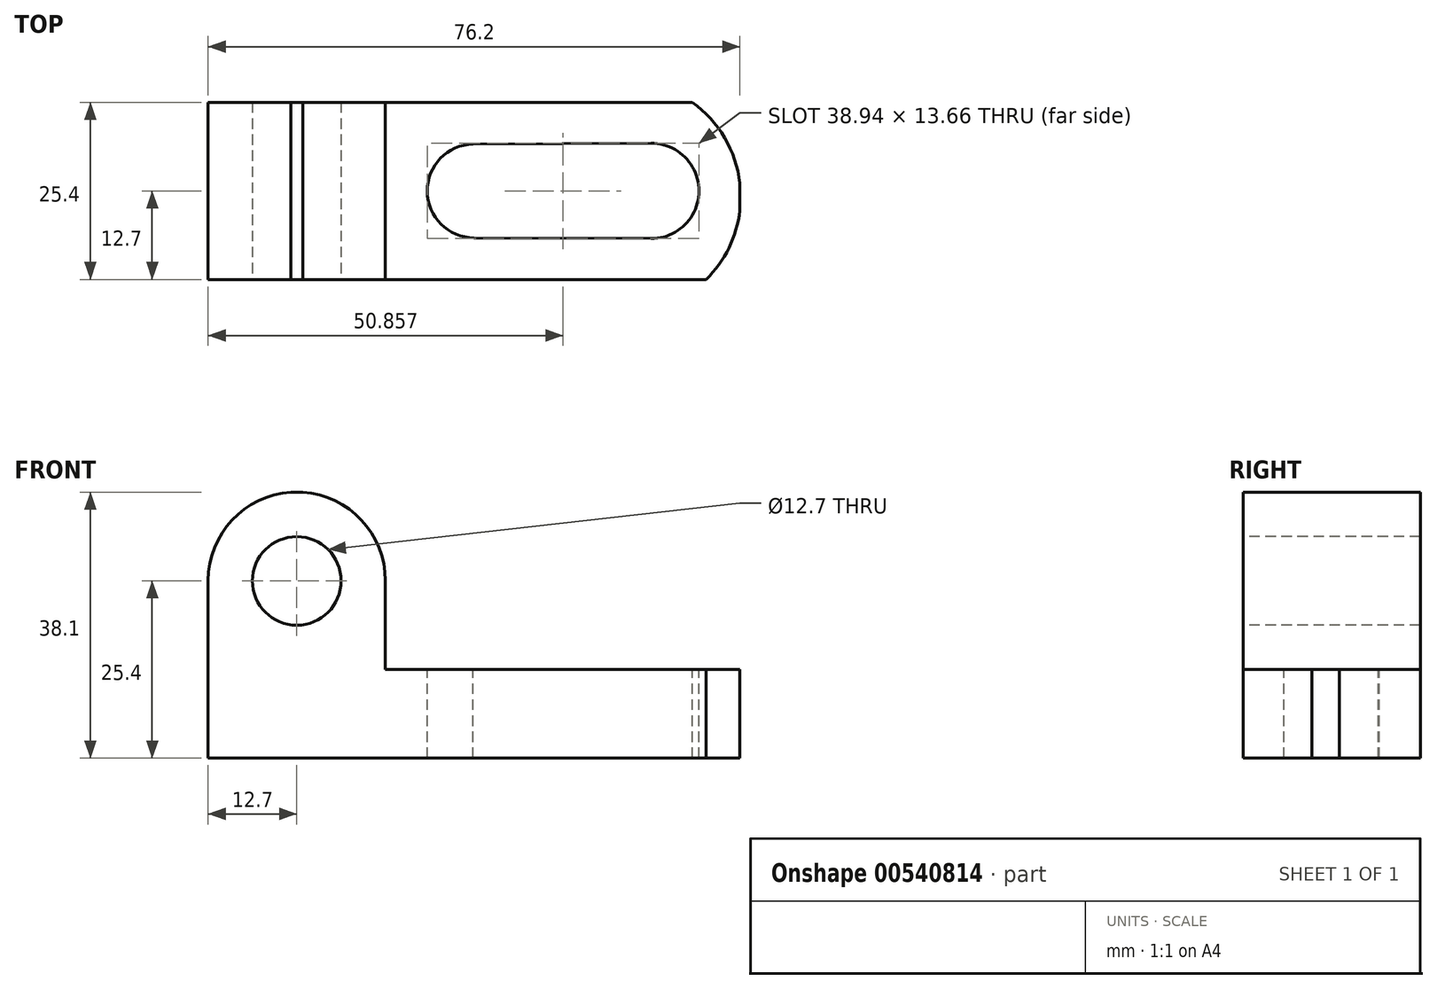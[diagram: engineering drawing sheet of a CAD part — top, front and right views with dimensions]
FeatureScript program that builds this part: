
annotation { "Feature Type Name" : "Feature", "Feature Type Description" : "" }
export const myFeature = defineFeature(function(context is Context, id is Id, definition is map)
    precondition{}
    {
        {
            var Q0;
            Q0=qCreatedBy(makeId("Front.planeOp"),FACE);
            var sketch = newSketch(context, id + "F0", { "sketchPlane" : qUnion([Q0])});
            skLineSegment(sketch, "E0", {"start": v(0, 0) * mm, "end": v(0, 38.1) * mm});
            skLineSegment(sketch, "E1", {"start": v(0, 38.1) * mm, "end": v(25.4, 38.1) * mm});
            skLineSegment(sketch, "E2", {"start": v(25.4, 38.1) * mm, "end": v(25.4, 12.7) * mm});
            skLineSegment(sketch, "E3", {"start": v(25.4, 12.7) * mm, "end": v(76.2, 12.7) * mm});
            skLineSegment(sketch, "E4", {"start": v(76.2, 12.7) * mm, "end": v(76.2, 0) * mm});
            skLineSegment(sketch, "E5", {"start": v(76.2, 0) * mm, "end": v(0, 0) * mm});
            skSolve(sketch);
        }
        {
            var Q0;
            Q0=makeQuery(id+"F0.imprint","IMPRINT",FACE,{"disambiguationData":[TD([[makeQuery(id+"F0.imprint","IMPRINT",EDGE,{"derivedFrom":sQuery(id+"F0.wireOp",EDGE,"E0")}),-1.0]])]});
            extrude(context, id + "F1", {"entities" : qUnion([Q0]), "depth" : 25.4 * mm, "offsetDistance" : 25.4 * mm});
        }
        {
            var Q0;
            Q0=makeQuery(id+"F1.opExtrude","CAP_FACE",FACE,{"disambiguationData":[OSD([sQuery(id+"F0.wireOp",EDGE,"E0"),sQuery(id+"F0.wireOp",EDGE,"E1"),sQuery(id+"F0.wireOp",EDGE,"E2"),sQuery(id+"F0.wireOp",EDGE,"E3"),sQuery(id+"F0.wireOp",EDGE,"E4"),sQuery(id+"F0.wireOp",EDGE,"E5")])],"isStart":false});
            var sketch = newSketch(context, id + "F2", { "sketchPlane" : qUnion([Q0])});
            skCircle(sketch, "E6", {"center": v(12.7, 25.4) * mm, "radius": 6.35 * mm});
            skArc(sketch, "E7", {"start": v(25.4, 25.4) * mm, "mid": v(12.7, 38.13) * mm, "end": v(0, 25.4) * mm});
            skSolve(sketch);
        }
        {
            var Q0;
            Q0=makeQuery(id+"F2.imprint","IMPRINT",FACE,{"disambiguationData":[TD([[makeQuery(id+"F2.imprint","IMPRINT",EDGE,{"derivedFrom":sQuery(id+"F2.wireOp",EDGE,"E6")}),1.0]])]});
            var Q1;
            {var subQ0=sQuery(id+"F2.wireOp",EDGE,"E7");var subQ3=makeQuery(id+"F1.opExtrude","CAP_EDGE",EDGE,{"disambiguationData":[OSD([sQuery(id+"F0.wireOp",EDGE,"E1")])],"isStart":false});var subQ4=makeQuery(id+"F2.imprint","INTERSECT",VERTEX,{"disambiguationData":[OD(0.0)],"derivedFrom":[subQ3,subQ0]});Q1=makeQuery(id+"F2.imprint","IMPRINT",FACE,{"disambiguationData":[TD([[makeQuery(id+"F2.imprint","IMPRINT",EDGE,{"disambiguationData":[TD([[subQ4,1.0]])],"derivedFrom":subQ0}),-1.0]])]});}
            var Q2;
            {var subQ0=sQuery(id+"F2.wireOp",EDGE,"E7");var subQ3=makeQuery(id+"F1.opExtrude","CAP_EDGE",EDGE,{"disambiguationData":[OSD([sQuery(id+"F0.wireOp",EDGE,"E1")])],"isStart":false});var subQ4=makeQuery(id+"F2.imprint","INTERSECT",VERTEX,{"disambiguationData":[OD(1.0)],"derivedFrom":[subQ3,subQ0]});Q2=makeQuery(id+"F2.imprint","IMPRINT",FACE,{"disambiguationData":[TD([[makeQuery(id+"F2.imprint","IMPRINT",EDGE,{"disambiguationData":[TD([[subQ4,-1.0]])],"derivedFrom":subQ0}),-1.0]])]});}
            extrude(context, id + "F3", {"entities" : qUnion([Q0, Q1, Q2]), "operationType" : NewBodyOperationType.REMOVE, "oppositeDirection" : true, "depth" : 25.4 * mm, "offsetDistance" : 25.4 * mm});
        }
        {
            var Q0;
            Q0=makeQuery(id+"F1.opExtrude","SWEPT_FACE",FACE,{"disambiguationData":[OSD([sQuery(id+"F0.wireOp",EDGE,"E3")])]});
            var sketch = newSketch(context, id + "F4", { "sketchPlane" : qUnion([Q0])});
            skCircle(sketch, "E8", {"center": v(38.1, -12.7) * mm, "radius": 6.71 * mm});
            skCircle(sketch, "E9", {"center": v(63.5, -12.7) * mm, "radius": 6.83 * mm});
            skLineSegment(sketch, "E10", {"start": v(37.95, -5.99) * mm, "end": v(63.47, -5.87) * mm});
            skLineSegment(sketch, "E11", {"start": v(63.47, -5.87) * mm, "end": v(63.47, -19.53) * mm});
            skLineSegment(sketch, "E12", {"start": v(63.47, -19.53) * mm, "end": v(38.07, -19.41) * mm});
            skLineSegment(sketch, "E13", {"start": v(38.07, -19.41) * mm, "end": v(37.95, -5.99) * mm});
            skSolve(sketch);
        }
        {
            var Q0;
            {var subQ0=sQuery(id+"F4.wireOp",EDGE,"E13");Q0=makeQuery(id+"F4.imprint","IMPRINT",FACE,{"disambiguationData":[TD([[makeQuery(id+"F4.imprint","IMPRINT",EDGE,{"derivedFrom":subQ0}),1.0]])]});}
            var Q1;
            {var subQ0=sQuery(id+"F4.wireOp",EDGE,"E13");Q1=makeQuery(id+"F4.imprint","IMPRINT",FACE,{"disambiguationData":[TD([[makeQuery(id+"F4.imprint","IMPRINT",EDGE,{"derivedFrom":subQ0}),-1.0]])]});}
            var Q2;
            {var subQ0=sQuery(id+"F4.wireOp",EDGE,"E12");Q2=makeQuery(id+"F4.imprint","IMPRINT",FACE,{"disambiguationData":[TD([[makeQuery(id+"F4.imprint","IMPRINT",EDGE,{"derivedFrom":subQ0}),-1.0]])]});}
            var Q3;
            {var subQ0=sQuery(id+"F4.wireOp",EDGE,"E11");Q3=makeQuery(id+"F4.imprint","IMPRINT",FACE,{"disambiguationData":[TD([[makeQuery(id+"F4.imprint","IMPRINT",EDGE,{"derivedFrom":subQ0}),-1.0]])]});}
            var Q4;
            {var subQ0=sQuery(id+"F4.wireOp",EDGE,"E11");Q4=makeQuery(id+"F4.imprint","IMPRINT",FACE,{"disambiguationData":[TD([[makeQuery(id+"F4.imprint","IMPRINT",EDGE,{"derivedFrom":subQ0}),1.0]])]});}
            extrude(context, id + "F5", {"entities" : qUnion([Q0, Q1, Q2, Q3, Q4]), "operationType" : NewBodyOperationType.REMOVE, "oppositeDirection" : true, "depth" : 25.4 * mm, "offsetDistance" : 25.4 * mm});
        }
        {
            var Q0;
            Q0=makeQuery(id+"F1.opExtrude","SWEPT_FACE",FACE,{"disambiguationData":[OSD([sQuery(id+"F0.wireOp",EDGE,"E3")])]});
            var sketch = newSketch(context, id + "F6", { "sketchPlane" : qUnion([Q0])});
            skArc(sketch, "E14", {"start": v(71.38, -25.4) * mm, "mid": v(76.26, -12.23) * mm, "end": v(69.36, 0) * mm});
            skSolve(sketch);
        }
        {
            var Q0;
            {var subQ0=sQuery(id+"F6.wireOp",EDGE,"E14");var subQ1=sQuery(id+"F0.wireOp",EDGE,"E3");var subQ2=makeQuery(id+"F1.opExtrude","CAP_EDGE",EDGE,{"disambiguationData":[OSD([subQ1])],"isStart":true});var subQ3=makeQuery(id+"F6.imprint","INTERSECT",VERTEX,{"derivedFrom":[subQ2,subQ0]});Q0=makeQuery(id+"F6.imprint","IMPRINT",FACE,{"disambiguationData":[TD([[makeQuery(id+"F6.imprint","IMPRINT",EDGE,{"disambiguationData":[TD([[subQ3,1.0]])],"derivedFrom":subQ0}),-1.0]])]});}
            var Q1;
            {var subQ0=sQuery(id+"F6.wireOp",EDGE,"E14");var subQ1=sQuery(id+"F0.wireOp",EDGE,"E3");var subQ2=makeQuery(id+"F1.opExtrude","CAP_EDGE",EDGE,{"disambiguationData":[OSD([subQ1])],"isStart":false});var subQ3=makeQuery(id+"F6.imprint","INTERSECT",VERTEX,{"derivedFrom":[subQ2,subQ0]});Q1=makeQuery(id+"F6.imprint","IMPRINT",FACE,{"disambiguationData":[TD([[makeQuery(id+"F6.imprint","IMPRINT",EDGE,{"disambiguationData":[TD([[subQ3,-1.0]])],"derivedFrom":subQ0}),-1.0]])]});}
            extrude(context, id + "F7", {"entities" : qUnion([Q0, Q1]), "operationType" : NewBodyOperationType.REMOVE, "oppositeDirection" : true, "depth" : 25.4 * mm, "offsetDistance" : 25.4 * mm});
        }
    });
